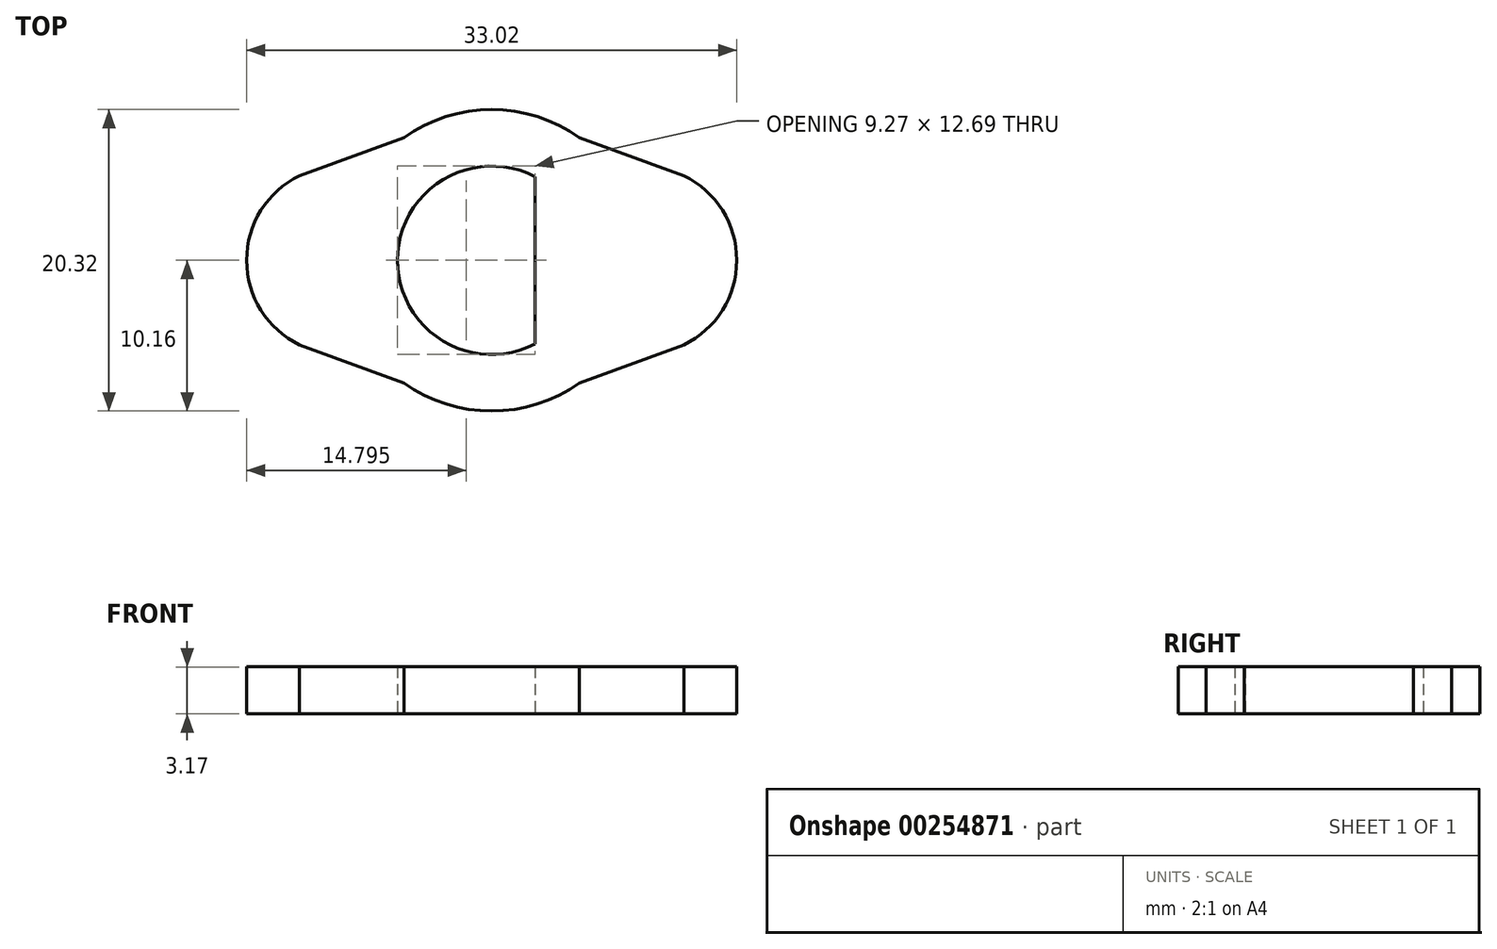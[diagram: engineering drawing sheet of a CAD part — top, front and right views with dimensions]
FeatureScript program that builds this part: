
annotation { "Feature Type Name" : "Feature", "Feature Type Description" : "" }
export const myFeature = defineFeature(function(context is Context, id is Id, definition is map)
    precondition{}
    {
        {
            var Q0;
            Q0=qCreatedBy(makeId("Top.planeOp"),FACE);
            var sketch = newSketch(context, id + "F0", { "sketchPlane" : qUnion([Q0])});
            skArc(sketch, "E0", {"start": v(0, 6.35) * mm, "mid": v(-4.5, 4.5) * mm, "end": v(-6.35, 0) * mm});
            skArc(sketch, "E1.0", {"start": v(0, 10.16) * mm, "mid": v(-3.1, 9.67) * mm, "end": v(-5.9, 8.26) * mm});
            skLineSegment(sketch, "E2", {"start": v(-12.95, 5.7) * mm, "end": v(-5.9, 8.26) * mm});
            skPoint(sketch, "E3.orphan", {"position": v(-28.63, 0) * mm});
            skArc(sketch, "E4.MirrorCS", {"start": v(0, -6.35) * mm, "mid": v(-4.5, -4.5) * mm, "end": v(-6.35, 0) * mm});
            skLineSegment(sketch, "E5.MirrorCS", {"start": v(-12.95, -5.7) * mm, "end": v(-5.9, -8.26) * mm});
            skArc(sketch, "E6.MirrorCS", {"start": v(0, -10.16) * mm, "mid": v(-3.1, -9.67) * mm, "end": v(-5.9, -8.26) * mm});
            skArc(sketch, "E7.MirrorCS", {"start": v(0, -10.16) * mm, "mid": v(3.1, -9.67) * mm, "end": v(5.9, -8.26) * mm});
            skLineSegment(sketch, "E8.MirrorCS", {"start": v(12.95, -5.7) * mm, "end": v(5.9, -8.26) * mm});
            skLineSegment(sketch, "E9.MirrorCS", {"start": v(12.95, 5.7) * mm, "end": v(5.9, 8.26) * mm});
            skArc(sketch, "E10.MirrorCS", {"start": v(0, 6.35) * mm, "mid": v(1.5, 6.17) * mm, "end": v(2.92, 5.64) * mm});
            skArc(sketch, "E11.MirrorCS", {"start": v(0, -6.35) * mm, "mid": v(1.5, -6.17) * mm, "end": v(2.92, -5.64) * mm});
            skArc(sketch, "E12.MirrorCS", {"start": v(0, 10.16) * mm, "mid": v(3.1, 9.67) * mm, "end": v(5.9, 8.26) * mm});
            skArc(sketch, "E13.trimOffspring", {"start": v(-11.69, 6.16) * mm, "mid": v(-15.16, 3.91) * mm, "end": v(-16.51, 0) * mm});
            skArc(sketch, "E14.trimOffspring", {"start": v(-11.69, -6.16) * mm, "mid": v(-15.16, -3.91) * mm, "end": v(-16.51, 0) * mm});
            skArc(sketch, "E15.trimOffspring", {"start": v(11.69, -6.16) * mm, "mid": v(15.16, -3.91) * mm, "end": v(16.5, 0) * mm});
            skArc(sketch, "E16.trimOffspring", {"start": v(11.69, 6.16) * mm, "mid": v(15.16, 3.91) * mm, "end": v(16.5, 0) * mm});
            skLineSegment(sketch, "E17", {"start": v(2.92, 0) * mm, "end": v(2.92, 5.64) * mm});
            skLineSegment(sketch, "E18.MirrorCS", {"start": v(2.92, 0) * mm, "end": v(2.92, -5.64) * mm});
            skPoint(sketch, "E19.orphan", {"position": v(2.92, 6.58) * mm});
            skPoint(sketch, "E20.orphan", {"position": v(2.92, -6.58) * mm});
            skSolve(sketch);
        }
        {
            var Q0;
            Q0=makeQuery(id+"F0.imprint","IMPRINT",FACE,{"disambiguationData":[TD([[makeQuery(id+"F0.imprint","IMPRINT",EDGE,{"derivedFrom":sQuery(id+"F0.wireOp",EDGE,"E0")}),-1.0]])]});
            extrude(context, id + "F1", {"entities" : qUnion([Q0]), "depth" : 3.17 * mm, "offsetDistance" : 25.4 * mm});
        }
    });
